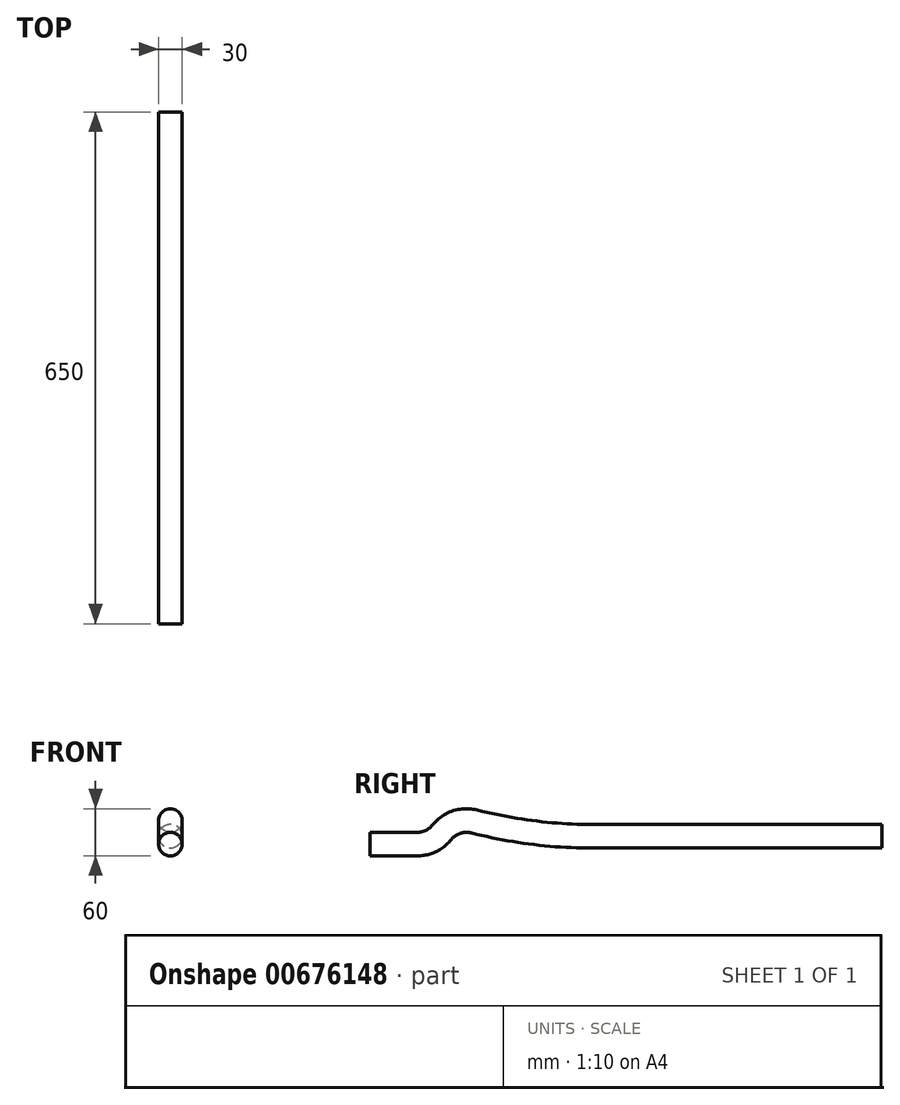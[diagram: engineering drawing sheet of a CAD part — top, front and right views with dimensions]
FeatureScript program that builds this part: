
annotation { "Feature Type Name" : "Feature", "Feature Type Description" : "" }
export const myFeature = defineFeature(function(context is Context, id is Id, definition is map)
    precondition{}
    {
        {
            var Q0;
            Q0=qCreatedBy(makeId("Right.planeOp"),FACE);
            var sketch = newSketch(context, id + "F0", { "sketchPlane" : qUnion([Q0])});
            skLineSegment(sketch, "E0", {"start": v(0, 0) * mm, "end": v(60, 0) * mm});
            skArc(sketch, "E1", {"start": v(60, 0) * mm, "mid": v(77.32, 3.94) * mm, "end": v(91.22, 15) * mm});
            skArc(sketch, "E2", {"start": v(91.22, 15) * mm, "mid": v(109.74, 27.93) * mm, "end": v(132.3, 28.77) * mm});
            skArc(sketch, "E3", {"start": v(132.3, 28.77) * mm, "mid": v(206.72, 14.7) * mm, "end": v(282.3, 10) * mm});
            skLineSegment(sketch, "E4", {"start": v(282.3, 10) * mm, "end": v(650, 10) * mm});
            skSolve(sketch);
        }
        {
            var Q0;
            Q0=qCreatedBy(makeId("Front.planeOp"),FACE);
            var sketch = newSketch(context, id + "F1", { "sketchPlane" : qUnion([Q0])});
            skCircle(sketch, "E5", {"center": v(0, 0) * mm, "radius": 15 * mm});
            skSolve(sketch);
        }
        {
            var Q0;
            Q0=sQuery(id+"F0.wireOp",VERTEX,"E4.start");
            var Q1;
            Q1=sQuery(id+"F0.wireOp",EDGE,"E4");
            cPlane(context, id + "F2", {"entities" : qUnion([Q0, Q1]), "cplaneType" : CPlaneType.CURVE_POINT, "offset" : 25 * mm, "width" : 150 * mm, "height" : 150 * mm});
        }
        {
            var Q0;
            Q0=makeQuery(id+"F1.imprint","IMPRINT",FACE,{"disambiguationData":[TD([[makeQuery(id+"F1.imprint","IMPRINT",EDGE,{"derivedFrom":sQuery(id+"F1.wireOp",EDGE,"E5")}),1.0]])]});
            var Q1;
            Q1=sQuery(id+"F0.wireOp",EDGE,"E0");
            var Q2;
            Q2=sQuery(id+"F0.wireOp",EDGE,"E1");
            var Q3;
            Q3=sQuery(id+"F0.wireOp",EDGE,"E2");
            var Q4;
            Q4=sQuery(id+"F0.wireOp",EDGE,"E3");
            var Q5;
            Q5=sQuery(id+"F0.wireOp",EDGE,"E4");
            sweep(context, id + "F3", {"profiles" : qUnion([Q0]), "path" : qUnion([Q1, Q2, Q3, Q4, Q5])});
        }
    });
